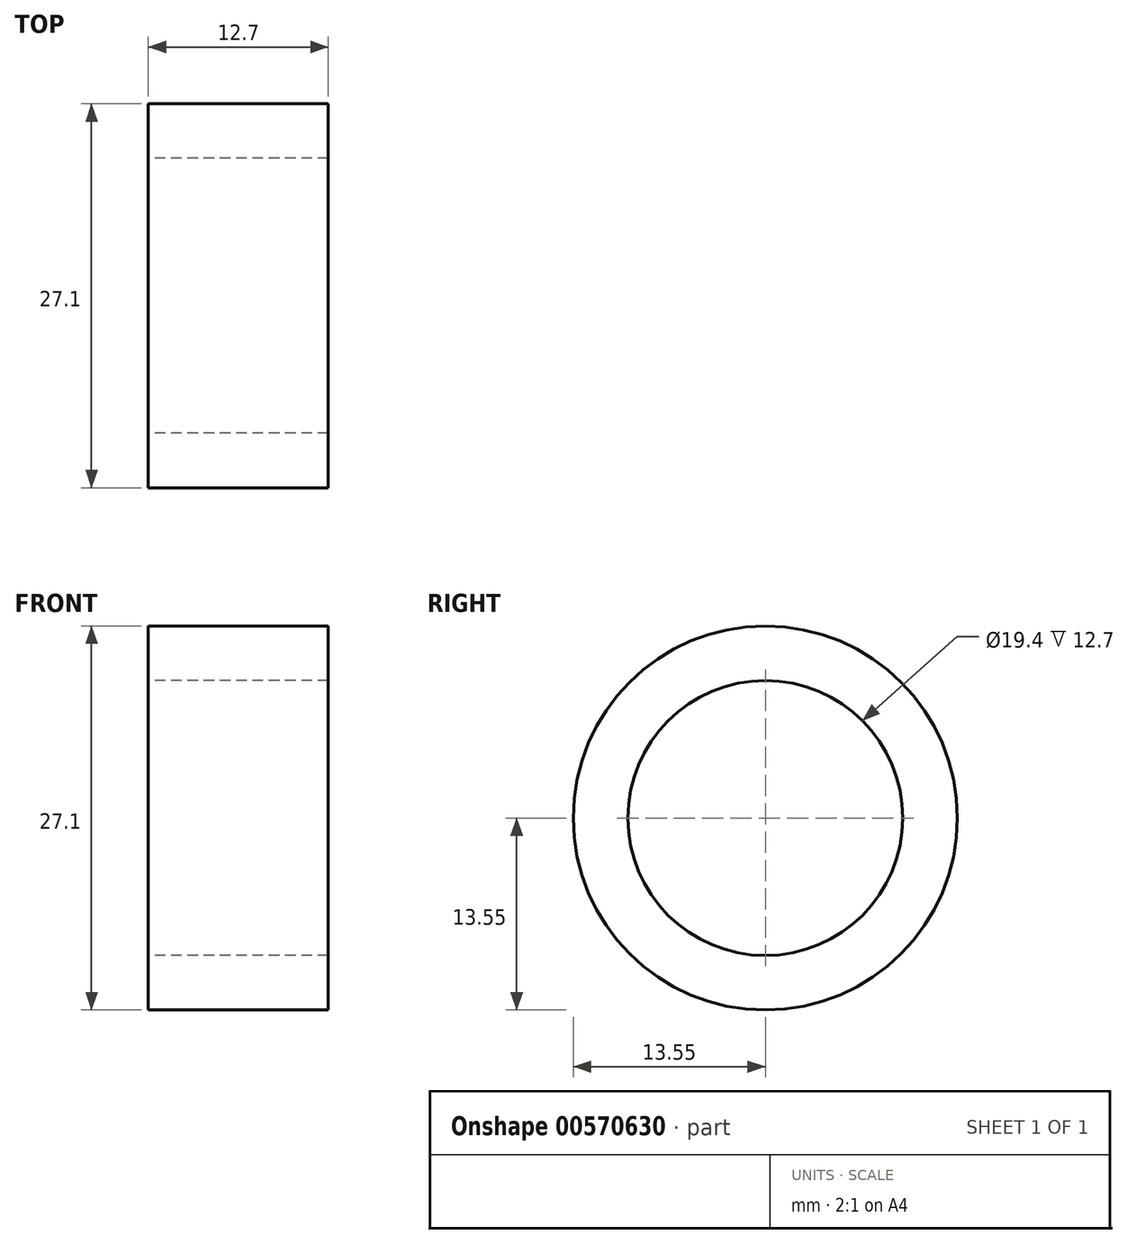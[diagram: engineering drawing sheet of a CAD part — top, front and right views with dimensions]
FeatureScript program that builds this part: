
annotation { "Feature Type Name" : "Feature", "Feature Type Description" : "" }
export const myFeature = defineFeature(function(context is Context, id is Id, definition is map)
    precondition{}
    {
        {
            var Q0;
            Q0=qCreatedBy(makeId("Top.planeOp"),FACE);
            var sketch = newSketch(context, id + "F0", { "sketchPlane" : qUnion([Q0])});
            skLineSegment(sketch, "E0", {"start": v(-54.45, 0) * mm, "end": v(-31.79, 0) * mm, "construction": true});
            skLineSegment(sketch, "E1.bottom", {"start": v(-49.35, 13.55) * mm, "end": v(-36.65, 13.55) * mm});
            skLineSegment(sketch, "E1.top", {"start": v(-49.35, 9.7) * mm, "end": v(-36.65, 9.7) * mm});
            skLineSegment(sketch, "E1.left", {"start": v(-49.35, 13.55) * mm, "end": v(-49.35, 9.7) * mm});
            skLineSegment(sketch, "E1.right", {"start": v(-36.65, 13.55) * mm, "end": v(-36.65, 9.7) * mm});
            skLineSegment(sketch, "E2.MirrorCS", {"start": v(-49.35, -13.55) * mm, "end": v(-36.65, -13.55) * mm});
            skLineSegment(sketch, "E3.MirrorCS", {"start": v(-49.35, -9.7) * mm, "end": v(-36.65, -9.7) * mm});
            skLineSegment(sketch, "E4.MirrorCS", {"start": v(-36.65, -13.55) * mm, "end": v(-36.65, -9.7) * mm});
            skLineSegment(sketch, "E5.MirrorCS", {"start": v(-49.35, -13.55) * mm, "end": v(-49.35, -9.7) * mm});
            skSolve(sketch);
        }
        {
            var Q0;
            Q0=makeQuery(id+"F0.imprint","IMPRINT",FACE,{"disambiguationData":[TD([[makeQuery(id+"F0.imprint","IMPRINT",EDGE,{"derivedFrom":sQuery(id+"F0.wireOp",EDGE,"E1.bottom")}),-1.0]])]});
            var Q1;
            Q1=sQuery(id+"F0.wireOp",EDGE,"E0");
            revolve(context, id + "F1", {"entities" : qUnion([Q0]), "axis" : qUnion([Q1]), "revolveType" : RevolveType.FULL});
        }
    });
